# Revit family: Drain_Floor_12_Inch_Diameter_Conical_Industrial-Zurn-Z1809_Double_Containment
name_source: partatom
category: Plumbing Fixtures
units: mm (PartAtom-declared; Revit-internal decimal feet)

## family parameters
Always vertical = Yes
Cut with Voids When Loaded = No
Maintain Annotation Orientation = No
OmniClass Number = 23.70.50.21.24
OmniClass Title = Waste Water Drains
Part Type = Normal
Room Calculation Point = No
Round Connector Dimension = Use Radius
Shared = No
Work Plane-Based = No

## types (6) — shared parameters
Assembly Code = D2030300
CW Connection = No
Default Elevation = 0' - 0"
Description = 12 Inch Round Industrial Conical Double Cointainment Sanitary Floor Drain
E_ Body Height = 0' - 8 5/8"
HW Connection = No
Manufacturer = Zurn Water, LLC
Manufacurer Brand = Zurn
Model = Z1809
Modified Date = February 25, 2026
Product Documentation Link = https://files.zurn.com
Product Page URL = https://www.zurn.com
Product data url = https://bimobject.com
Top Diameter = 0' - 11 13/16"
URL = www.zurn.com
Vent Connection = No
Waste Connection = Yes

## per-type parameters (varying)
| type | Main Material | Nominal Outlet Radius | Outlet Outer Radius | Type Comments |
| Z1809-2 Inch No-Hub Outlet | Steel - Zurn - Stainless Type 304 (CF8) | 0' - 1" | 0' - 1 1/8" | Z1809-2NH Outlet (Type 304 CF8) |
| Z1809-3 Inch No-Hub Outlet | Steel - Zurn - Stainless Type 304 (CF8) | 0' - 1 1/2" | 0' - 1 5/8" | Z1809-3NH Outlet (Type 304 CF8) |
| Z1809-4 Inch No-Hub Outlet | Steel - Zurn - Stainless Type 304 (CF8) | 0' - 2" | 0' - 2 1/8" | Z1809-3NH Outlet (Type 304 CF8) |
| ZM1809-2 Inch No-Hub Outlet | Steel - Zurn - Stainless (Type 316 CF8M) | 0' - 1" | 0' - 1 1/8" | ZM1809-2NH Outlet (Type 316 CF8M) |
| ZM1809-3 Inch No-Hub Outlet | Steel - Zurn - Stainless (Type 316 CF8M) | 0' - 1 1/2" | 0' - 1 5/8" | ZM1809-3NH Outlet (Type 316 CFM8) |
| ZM1809-4 Inch No-Hub Outlet | Steel - Zurn - Stainless (Type 316 CF8M) | 0' - 2" | 0' - 2 1/8" | ZM1809-3NH Outlet (Type 316 CF8M) |

## geometry (parser evidence)
native form markers: Sweep x3
no freeform markers — native parametric forms only
